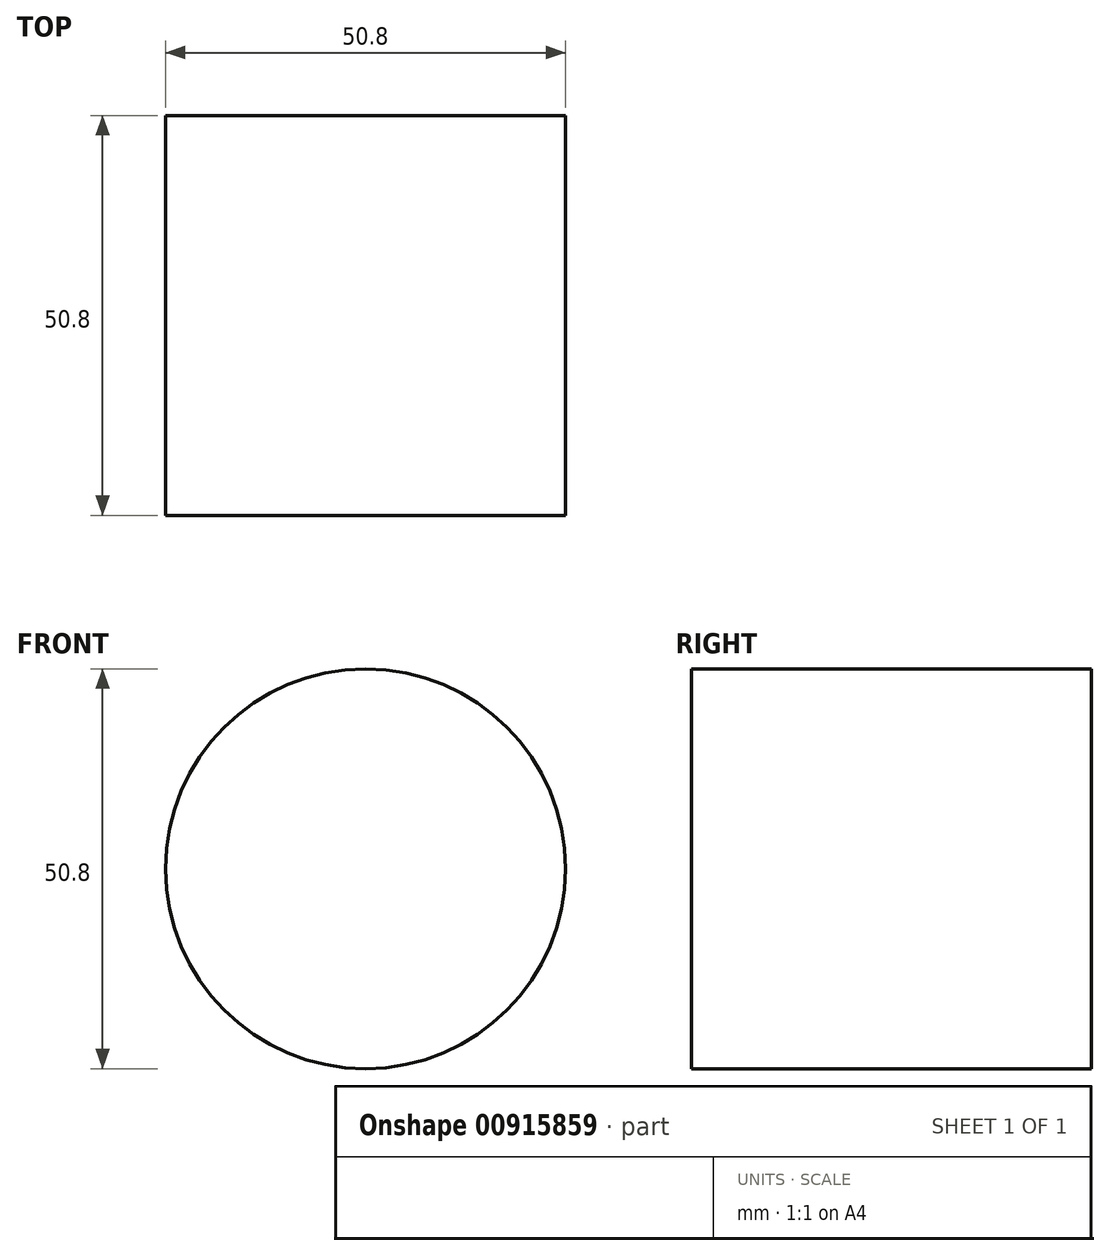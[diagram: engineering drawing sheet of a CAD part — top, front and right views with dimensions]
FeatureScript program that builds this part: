
annotation { "Feature Type Name" : "Feature", "Feature Type Description" : "" }
export const myFeature = defineFeature(function(context is Context, id is Id, definition is map)
    precondition{}
    {
        {
            var Q0;
            Q0=qCreatedBy(makeId("Front.planeOp"),FACE);
            var sketch = newSketch(context, id + "F0", { "sketchPlane" : qUnion([Q0])});
            skCircle(sketch, "E0", {"center": v(0, 0) * mm, "radius": 25.4 * mm});
            skSolve(sketch);
        }
        {
            var Q0;
            Q0 = qSketchRegion(id + "F0", true);
            extrude(context, id + "F1", {"entities" : qUnion([Q0]), "depth" : 50.8 * mm, "offsetDistance" : 25.4 * mm});
        }
    });
